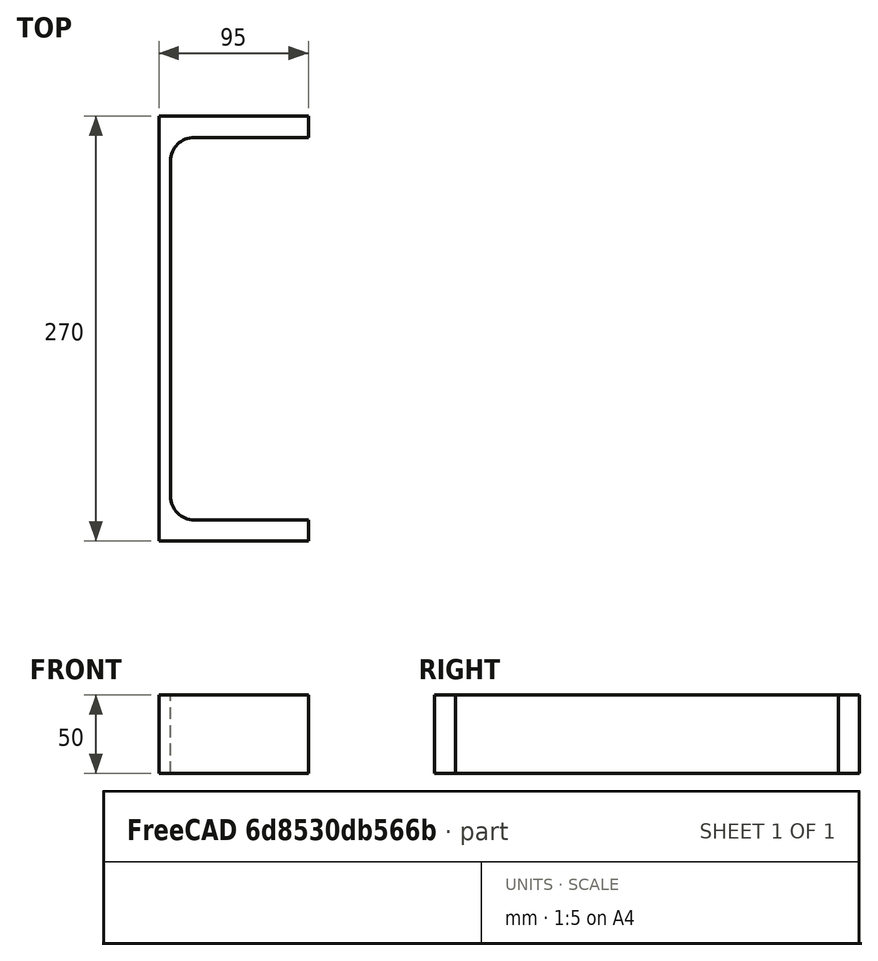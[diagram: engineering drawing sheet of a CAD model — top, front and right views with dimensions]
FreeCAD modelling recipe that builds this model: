
FCSTD DOCUMENT  (FreeCAD 0.20R29410 (Git))
Label: UPE-Profile 270 DIN1026-2 S235JR
License: All rights reserved
LicenseURL: http://en.wikipedia.org/wiki/All_rights_reserved
objects: Sketcher::SketchObject×1, Part::Extrusion×1
note: 2 computed .brp shape members not serialized (recipe doc carries the construction recipe); baked Part::Feature solids carry a one-line shape summary decoded from their .brp

FEATURE [Sketcher::SketchObject] Sketch
  FullyConstrained = true
  MapMode = 5
  sketch-geometry (10):
    g0: LineSegment StartX=7.5 StartY=-106.5 StartZ=0 EndX=7.5 EndY=106.5 EndZ=0
    g1: LineSegment StartX=22.5 StartY=121.5 StartZ=0 EndX=95 EndY=121.5 EndZ=0
    g2: LineSegment StartX=95 StartY=121.5 StartZ=0 EndX=95 EndY=135 EndZ=0
    g3: LineSegment StartX=95 StartY=-135 StartZ=0 EndX=95 EndY=-121.5 EndZ=0
    g4: LineSegment StartX=95 StartY=-121.5 StartZ=0 EndX=22.5 EndY=-121.5 EndZ=0
    g5: ArcOfCircle CenterX=22.5 CenterY=106.5 CenterZ=0 NormalX=0 NormalY=0 NormalZ=1 AngleXU=0 Radius=15 StartAngle=1.5708 EndAngle=3.14159
    g6: ArcOfCircle CenterX=22.5 CenterY=-106.5 CenterZ=0 NormalX=0 NormalY=0 NormalZ=1 AngleXU=0 Radius=15 StartAngle=3.14159 EndAngle=4.71239
    g7: LineSegment StartX=95 StartY=-135 StartZ=0 EndX=0 EndY=-135 EndZ=0
    g8: LineSegment StartX=0 StartY=-135 StartZ=0 EndX=0 EndY=135 EndZ=0
    g9: LineSegment StartX=0 StartY=135 StartZ=0 EndX=95 EndY=135 EndZ=0
  constraints (27):
    c: Vertical(g0)
    c: Coincident(g2,g1)
    c: Vertical(g2)
    c: Vertical(g3)
    c: Coincident(g4,g3)
    c: Horizontal(g4)
    c: Tangent(g1,g5) = 1.5708
    c: Tangent(g0,g5) = 1.5708
    c: Tangent(g0,g6) = 1.5708
    c: Tangent(g4,g6) = 1.5708
    c: Symmetric(g2,g3,g-1)
    c: DistanceY(g2) = 13.5
    c: Radius(g5) = 15
    c: Coincident(g3,g7)
    c: PointOnObject(g7,g-2)
    c: Horizontal(g7)
    c: Coincident(g7,g8)
    c: PointOnObject(g8,g-2)
    c: Coincident(g8,g9)
    c: Coincident(g9,g2)
    c: Horizontal(g9)
    c: Distance(g-1,g0) = 7.5
    c: DistanceX(g9,g9) = 95
    c: Horizontal(g1)
    c: Equal(g3,g2)
    c: Equal(g5,g6)
    c: DistanceY(g3,g2) = 270
FEATURE [Part::Extrusion] Extrude  label="UPE-Profile 270 DIN1026-2 S235JR"
  Base = -> Sketch
  Dir = (0,0,50)
  DirMode = 0
  FaceMakerClass = Part::FaceMakerExtrusion
  LengthFwd = 0
  LengthRev = 0
  Solid = true
  Symmetric = false
